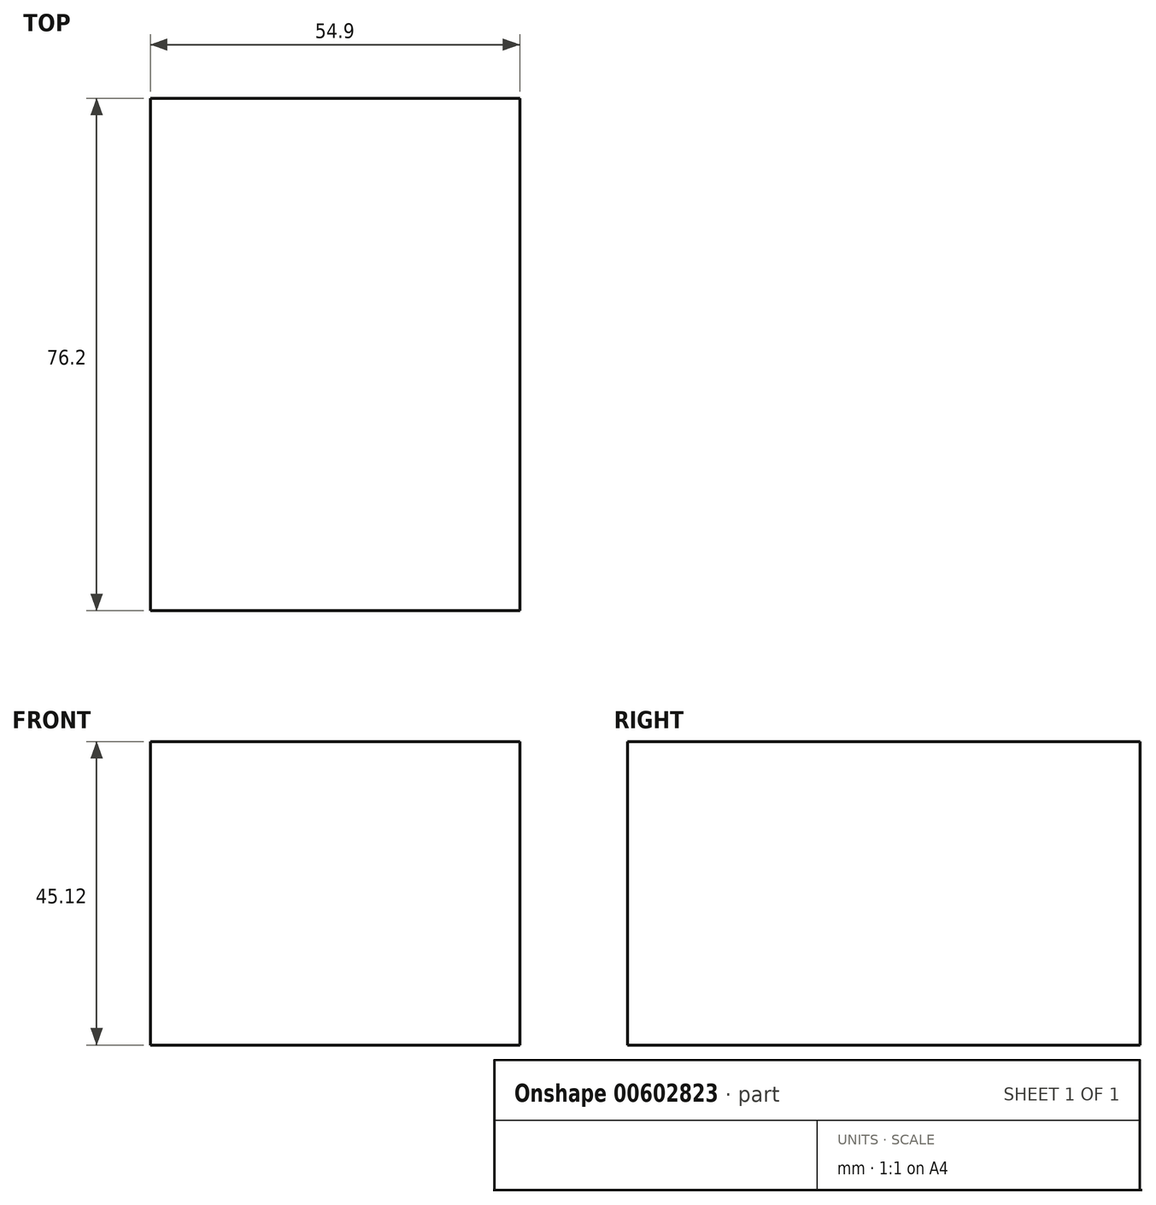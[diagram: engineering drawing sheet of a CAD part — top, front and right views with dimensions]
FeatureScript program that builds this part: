
annotation { "Feature Type Name" : "Feature", "Feature Type Description" : "" }
export const myFeature = defineFeature(function(context is Context, id is Id, definition is map)
    precondition{}
    {
        {
            var Q0;
            Q0=qCreatedBy(makeId("Front.planeOp"),FACE);
            var sketch = newSketch(context, id + "F0", { "sketchPlane" : qUnion([Q0])});
            skLineSegment(sketch, "E0.bottom", {"start": v(0, 0) * mm, "end": v(-54.9, 0) * mm});
            skLineSegment(sketch, "E0.top", {"start": v(0, 45.12) * mm, "end": v(-54.9, 45.12) * mm});
            skLineSegment(sketch, "E0.left", {"start": v(0, 0) * mm, "end": v(0, 45.12) * mm});
            skLineSegment(sketch, "E0.right", {"start": v(-54.9, 0) * mm, "end": v(-54.9, 45.12) * mm});
            skSolve(sketch);
        }
        {
            var Q0;
            Q0=makeQuery(id+"F0.imprint","IMPRINT",FACE,{"disambiguationData":[TD([[makeQuery(id+"F0.imprint","IMPRINT",EDGE,{"derivedFrom":sQuery(id+"F0.wireOp",EDGE,"E0.bottom")}),-1.0]])]});
            extrude(context, id + "F1", {"entities" : qUnion([Q0]), "depth" : 76.2 * mm, "offsetDistance" : 25.4 * mm});
        }
    });
